# Revit family: Плита многопустотная
name_source: partatom
category: Обобщенные модели
revit_build: Autodesk Revit Structure 2016 (Build: 20150220_1215(x64)
units: mm (PartAtom-declared; Revit-internal decimal feet)

## family parameters
Всегда вертикально = Нет
Может служить основой для арматурных стержней = Нет
На основе рабочей плоскости = Нет
Общий = Нет
При загрузке вырезать с полостями = Нет
Точка расчета площади = Нет

## types (10) — shared parameters
H = 220 мм
URL = http://www.beton1.ru
_Материал = Бетон - Сборный железобетон - 35 МПa
Высота плиты = -220 мм
вид1000 = Нет

## per-type parameters (varying)
| type | Длина плиты | Изготовитель | Комментарии к типоразмеру | Описание | вид1200 | вид1500 | ширина плиты |
| ПК12 | 6000 мм | Серия 1.141-1 выпуск 63 | ПК60.12-8АтVт | 2,10 | Да | Нет | 1200 мм |
| ПБ15.53 | 5300 мм | Серия. .. | ПК60.15-8АтVт | 2,80 | Нет | Да | 1500 мм |
| ПБ12.60 | 6000 мм | Серия. .. | ПК60.15-8АтVт | 2,80 | Да | Нет | 1200 мм |
| ПБ15.74 | 7400 мм | Серия. .. | ПК60.15-8АтVт | 2,80 | Нет | Да | 1500 мм |
| ПБ15.60 | 6000 мм | Серия. .. | ПК60.15-8АтVт | 2,80 | Нет | Да | 1500 мм |
| ПБ15.55 | 5500 мм | Серия. .. | ПК60.15-8АтVт | 2,80 | Нет | Да | 1500 мм |
| ПБ12.21 | 2100 мм | Серия. .. | ПК60.15-8АтVт | 2,80 | Да | Нет | 1200 мм |
| ПБ15.21 | 2100 мм | Серия. .. | ПК60.15-8АтVт | 2,80 | Нет | Да | 1500 мм |
| ПБ12.69 | 6900 мм | Серия. .. | ПК60.15-8АтVт | 2,80 | Да | Нет | 1200 мм |
| ПБ15.69 | 6900 мм | Серия. .. | ПК60.15-8АтVт | 2,80 | Нет | Да | 1500 мм |

## geometry (parser evidence)
native form markers: Blend x6
no freeform markers — native parametric forms only
